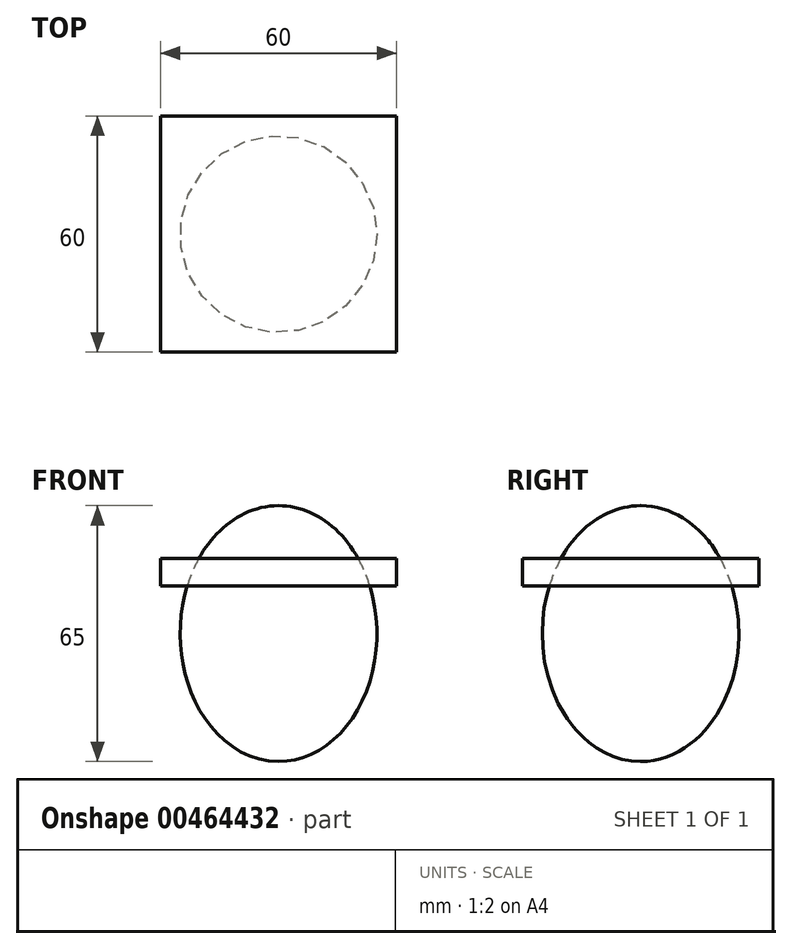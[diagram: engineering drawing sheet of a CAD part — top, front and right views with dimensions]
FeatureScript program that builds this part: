
annotation { "Feature Type Name" : "Feature", "Feature Type Description" : "" }
export const myFeature = defineFeature(function(context is Context, id is Id, definition is map)
    precondition{}
    {
        {
            var Q0;
            Q0=qCreatedBy(makeId("Front.planeOp"),FACE);
            var sketch = newSketch(context, id + "F0", { "sketchPlane" : qUnion([Q0])});
            skEllipticalArc(sketch, "E0", {});
            skLineSegment(sketch, "E1", {"start": v(0, 0) * mm, "end": v(0, 32.5) * mm});
            skLineSegment(sketch, "E2", {"start": v(0, 32.5) * mm, "end": v(0, -32.5) * mm});
            skLineSegment(sketch, "E3", {"start": v(0, 0) * mm, "end": v(25, 0) * mm});
            const initialGuessF0  = {"E0": [0, 0, 0, -1, 0.0325, 0.025, 0, 3.141592653589793]};
            skSetInitialGuess(sketch, initialGuessF0);
            skSolve(sketch);
        }
        {
            var Q0;
            {var subQ0=sQuery(id+"F0.wireOp",EDGE,"E0");Q0=makeQuery(id+"F0.imprint","IMPRINT",FACE,{"disambiguationData":[TD([[makeQuery(id+"F0.imprint","IMPRINT",EDGE,{"derivedFrom":subQ0}),1.0]])]});}
            var Q1;
            Q1=sQuery(id+"F0.wireOp",EDGE,"E2");
            revolve(context, id + "F1", {"entities" : qUnion([Q0]), "axis" : qUnion([Q1]), "revolveType" : RevolveType.FULL});
        }
        {
            var Q0;
            Q0=qCreatedBy(makeId("Top.planeOp"),FACE);
            cPlane(context, id + "F2", {"entities" : qUnion([Q0]), "cplaneType" : CPlaneType.OFFSET, "offset" : 19.05 * mm, "width" : 152.4 * mm, "height" : 152.4 * mm});
        }
        {
            var Q0;
            Q0=qCreatedBy(id+"F2.planeOp",FACE);
            var sketch = newSketch(context, id + "F3", { "sketchPlane" : qUnion([Q0])});
            skLineSegment(sketch, "E4.bottom", {"start": v(30, -30) * mm, "end": v(-30, -30) * mm});
            skLineSegment(sketch, "E4.top", {"start": v(30, 30) * mm, "end": v(-30, 30) * mm});
            skLineSegment(sketch, "E4.left", {"start": v(30, -30) * mm, "end": v(30, 30) * mm});
            skLineSegment(sketch, "E4.right", {"start": v(-30, -30) * mm, "end": v(-30, 30) * mm});
            skPoint(sketch, "E4.middle", {"position": v(0, 0) * mm});
            skSolve(sketch);
        }
        {
            var Q0;
            Q0=qSketchRegion(id+"F3",true);
            extrude(context, id + "F4", {"entities" : qUnion([Q0]), "oppositeDirection" : true, "depth" : 7 * mm});
        }
    });
